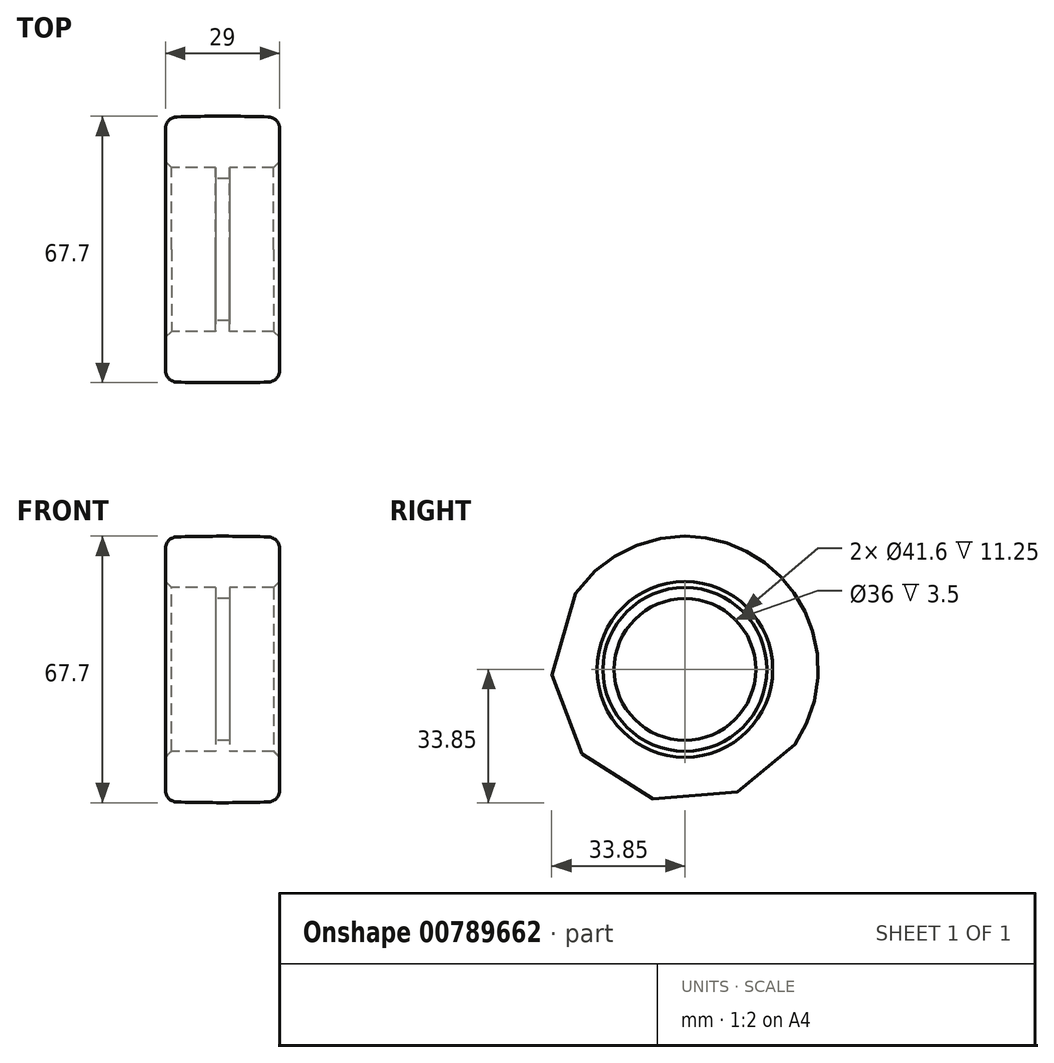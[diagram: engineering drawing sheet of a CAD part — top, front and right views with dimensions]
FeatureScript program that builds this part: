
annotation { "Feature Type Name" : "Feature", "Feature Type Description" : "" }
export const myFeature = defineFeature(function(context is Context, id is Id, definition is map)
    precondition{}
    {
        {
            var Q0;
            Q0=qCreatedBy(makeId("Front.planeOp"),FACE);
            var sketch = newSketch(context, id + "F0", { "sketchPlane" : qUnion([Q0])});
            skLineSegment(sketch, "E0", {"start": v(0, 0) * mm, "end": v(38.88, 0) * mm, "construction": true});
            skLineSegment(sketch, "E1", {"start": v(0, 44.66) * mm, "end": v(0, 64.22) * mm, "construction": true});
            skPoint(sketch, "E2", {"position": v(0, 33.85) * mm});
            skLineSegment(sketch, "E3", {"start": v(14.5, 30.7) * mm, "end": v(14.5, 20.8) * mm});
            skLineSegment(sketch, "E4", {"start": v(14.5, 20.8) * mm, "end": v(1.75, 20.8) * mm});
            skLineSegment(sketch, "E5", {"start": v(1.75, 20.8) * mm, "end": v(1.75, 18) * mm});
            skLineSegment(sketch, "E6", {"start": v(1.75, 18) * mm, "end": v(0, 18) * mm});
            skLineSegment(sketch, "E7.MirrorCS", {"start": v(-14.5, 30.7) * mm, "end": v(-14.5, 20.8) * mm});
            skArc(sketch, "E8", {"start": v(11.58, 33.7) * mm, "mid": v(0, 33.85) * mm, "end": v(-11.58, 33.7) * mm});
            skPoint(sketch, "E9.visualSharp", {"position": v(-14.5, 33.6) * mm});
            skArc(sketch, "E9.filletArc", {"start": v(-11.58, 33.7) * mm, "mid": v(-13.65, 32.78) * mm, "end": v(-14.5, 30.7) * mm});
            skPoint(sketch, "E10.visualSharp", {"position": v(14.5, 33.6) * mm});
            skArc(sketch, "E10.filletArc", {"start": v(14.5, 30.7) * mm, "mid": v(13.65, 32.78) * mm, "end": v(11.58, 33.7) * mm});
            skLineSegment(sketch, "E11.MirrorCS", {"start": v(-1.75, 18) * mm, "end": v(0, 18) * mm});
            skLineSegment(sketch, "E12.MirrorCS", {"start": v(-1.75, 20.8) * mm, "end": v(-1.75, 18) * mm});
            skLineSegment(sketch, "E13.MirrorCS", {"start": v(-14.5, 20.8) * mm, "end": v(-1.75, 20.8) * mm});
            skSolve(sketch);
        }
        {
            var Q0;
            Q0 = qSketchRegion(id + "F0", true);
            var Q1;
            Q1=sQuery(id+"F0.wireOp",EDGE,"E0");
            revolve(context, id + "F1", {"surfaceOperationType" : NewSurfaceOperationType.NEW, "entities" : qUnion([Q0]), "axis" : qUnion([Q1]), "revolveType" : RevolveType.FULL});
        }
        {
            var Q0;
            Q0=makeQuery(id+"F1.opRevolve","SWEPT_EDGE",EDGE,{"disambiguationData":[OSD([sQuery(id+"F0.wireOp",EDGE,"E7.MirrorCS"),sQuery(id+"F0.wireOp",EDGE,"E13.MirrorCS")])]});
            var Q1;
            Q1=makeQuery(id+"F1.opRevolve","SWEPT_EDGE",EDGE,{"disambiguationData":[OSD([sQuery(id+"F0.wireOp",EDGE,"E3"),sQuery(id+"F0.wireOp",EDGE,"E4")])]});
            chamfer(context, id + "F2", {"entities" : qUnion([Q0, Q1]), "width" : 1.5 * mm, "tangentPropagation" : true});
        }
    });
